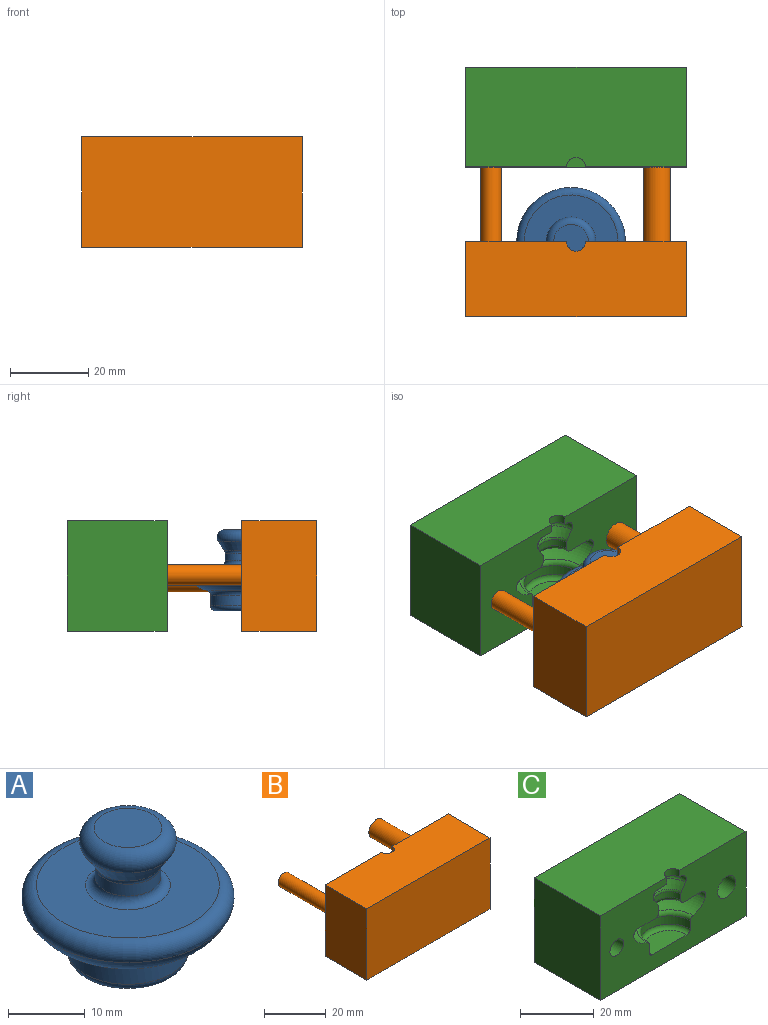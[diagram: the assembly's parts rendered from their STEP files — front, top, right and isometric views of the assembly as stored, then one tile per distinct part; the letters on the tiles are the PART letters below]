
ASSEMBLY  parts=3 mates=2
PART A: 13 faces, bbox 30.9x30.9x20.7 mm
  f0: torus R=7.92mm, axis (0,0,1), area 444.9mm2, adj f8,f12
  f1: plane 23.88x23.88mm, normal (0,0,1), area 351.7mm2, adj f8,f9
  f2: cylinder r=4.27mm len=8.53mm, axis (0,0,1), area 50.4mm2, adj f9,f10
  f3: cone r=4.27mm half-angle=33.2deg, axis (0,0,1), area 93mm2, adj f7,f10
  f4: plane 8.85x8.85mm, normal (0,0,1), area 61.5mm2, adj f7
  f5: plane 13.31x13.31mm, normal (0,0,-1), area 139.1mm2, adj f11
  f6: cylinder r=7.92mm len=15.85mm, axis (0,0,1), area 135.9mm2, adj f11,f12
  f7: torus R=4.42mm, axis (0,0,-1), area 149.2mm2, adj f3,f4
  f8: torus R=11.94mm, axis (0,0,-1), area 320.4mm2, adj f0,f1
  f9: torus R=5.54mm, axis (0,0,-1), area 59.3mm2, adj f1,f2
  f10: torus R=5.54mm, axis (0,0,1), area 20.1mm2, adj f2,f3
  f11: torus R=6.65mm, axis (0,0,-1), area 93.5mm2, adj f5,f6
  f12: torus R=9.19mm, axis (0,0,1), area 93mm2, adj f0,f6
PART B: 24 faces, bbox 56.2x44.5x28.2 mm
  f0: plane 56.17x28.17mm, normal (0,1,0), area 1176.1mm2, adj f1,f2,f3,f4,f6,f8,f10,f11
  f1: plane 56.17x19.05mm, normal (0,0,1), area 1061.1mm2, adj f0,f2,f4,f5,f23
  f2: plane 28.17x19.05mm, normal (-1,0,0), area 536.6mm2, adj f0,f1,f3,f5
  f3: plane 56.17x19.05mm, normal (0,0,-1), area 1070mm2, adj f0,f2,f4,f5
  f4: plane 28.17x19.05mm, normal (1,0,0), area 536.6mm2, adj f0,f1,f3,f5
  f5: plane 56.17x28.17mm, normal (0,-1,0), area 1582.3mm2, adj f1,f2,f3,f4
  f6: cylinder r=2.62mm len=25.4mm, axis (0,-1,0), area 418mm2, adj f0,f7
  f7: plane 5.24x5.24mm, normal (0,1,0), area 21.6mm2, adj f6
  f8: cylinder r=3.43mm len=25.4mm, axis (0,-1,0), area 547mm2, adj f0,f9
  f9: plane 6.85x6.85mm, normal (0,1,0), area 36.9mm2, adj f8
  f10: torus R=7.92mm, axis (0,0,1), area 222.5mm2, adj f0,f18,f22
  f11: plane 23.88x11.94mm, normal (0,0,-1), area 175.8mm2, adj f0,f18,f19
  f12: cylinder r=4.27mm len=8.53mm, axis (0,0,1), area 25.2mm2, adj f0,f19,f20
  f13: cone r=4.27mm half-angle=33.2deg, axis (0,0,1), area 46.5mm2, adj f0,f17,f20
  f14: plane 8.85x4.43mm, normal (0,0,-1), area 21.8mm2, adj f0,f17,f23
  f15: plane 13.31x6.66mm, normal (0,0,1), area 69.6mm2, adj f0,f21
  f16: cylinder r=7.92mm len=15.85mm, axis (0,0,1), area 67.9mm2, adj f0,f21,f22
  f17: torus R=4.42mm, axis (0,0,-1), area 74.6mm2, adj f0,f13,f14
  f18: torus R=11.94mm, axis (0,0,-1), area 160.2mm2, adj f0,f10,f11
  f19: torus R=5.54mm, axis (0,0,-1), area 29.6mm2, adj f0,f11,f12
  f20: torus R=5.54mm, axis (0,0,1), area 10mm2, adj f0,f12,f13
  f21: torus R=6.65mm, axis (0,0,-1), area 46.8mm2, adj f0,f15,f16
  f22: torus R=9.19mm, axis (0,0,1), area 46.5mm2, adj f0,f10,f16
  f23: cylinder r=2.38mm len=4.76mm, axis (0,0,1), area 17.3mm2, adj f0,f1,f14
PART C: 22 faces, bbox 56.2x25.4x28.2 mm
  f0: plane 56.17x28.17mm, normal (0,-1,0), area 1176.1mm2, adj f1,f2,f3,f4,f5,f6,f8,f9
  f1: plane 56.17x25.4mm, normal (0,0,1), area 1417.8mm2, adj f0,f2,f6,f7,f21
  f2: plane 28.17x25.4mm, normal (-1,0,0), area 715.5mm2, adj f0,f1,f3,f7
  f3: plane 56.17x25.4mm, normal (0,0,-1), area 1426.7mm2, adj f0,f2,f6,f7
  f4: cylinder r=2.62mm len=25.4mm, axis (0,-1,0), area 418mm2, adj f0,f7
  f5: cylinder r=3.43mm len=25.4mm, axis (0,-1,0), area 547mm2, adj f0,f7
  f6: plane 28.17x25.4mm, normal (1,0,0), area 715.5mm2, adj f0,f1,f3,f7
  f7: plane 56.17x28.17mm, normal (0,1,0), area 1523.8mm2, adj f1,f2,f3,f4,f5,f6
  f8: torus R=7.92mm, axis (0,0,1), area 222.5mm2, adj f0,f16,f20
  f9: plane 23.88x11.94mm, normal (0,0,-1), area 175.8mm2, adj f0,f16,f17
  f10: cylinder r=4.27mm len=8.53mm, axis (0,0,1), area 25.2mm2, adj f0,f17,f18
  f11: cone r=4.27mm half-angle=33.2deg, axis (0,0,1), area 46.5mm2, adj f0,f15,f18
  f12: plane 8.85x4.43mm, normal (0,0,-1), area 21.8mm2, adj f0,f15,f21
  f13: plane 13.31x6.66mm, normal (0,0,1), area 69.6mm2, adj f0,f19
  f14: cylinder r=7.92mm len=15.85mm, axis (0,0,1), area 67.9mm2, adj f0,f19,f20
  f15: torus R=4.42mm, axis (0,0,-1), area 74.6mm2, adj f0,f11,f12
  f16: torus R=11.94mm, axis (0,0,-1), area 160.2mm2, adj f0,f8,f9
  f17: torus R=5.54mm, axis (0,0,-1), area 29.6mm2, adj f0,f9,f10
  f18: torus R=5.54mm, axis (0,0,1), area 10mm2, adj f0,f10,f11
  f19: torus R=6.65mm, axis (0,0,-1), area 46.8mm2, adj f0,f13,f14
  f20: torus R=9.19mm, axis (0,0,1), area 46.5mm2, adj f0,f8,f14
  f21: cylinder r=2.38mm len=4.76mm, axis (0,0,1), area 17.3mm2, adj f0,f1,f12
PLACE A t=(-2.97,-16.93,-9.15)mm
PLACE B t=(-2.97,-16.93,-9.15)mm fixed
PLACE C t=(-2.97,2.12,-9.15)mm
MATE slider B.f6 <-> C.f4  axis (0,1,0) through (-23.36,8.47,-1.95)mm
MATE fastened A.f0 <-> B.f10  axis (0,0,-1) through (-2.97,-16.93,-11.14)mm
